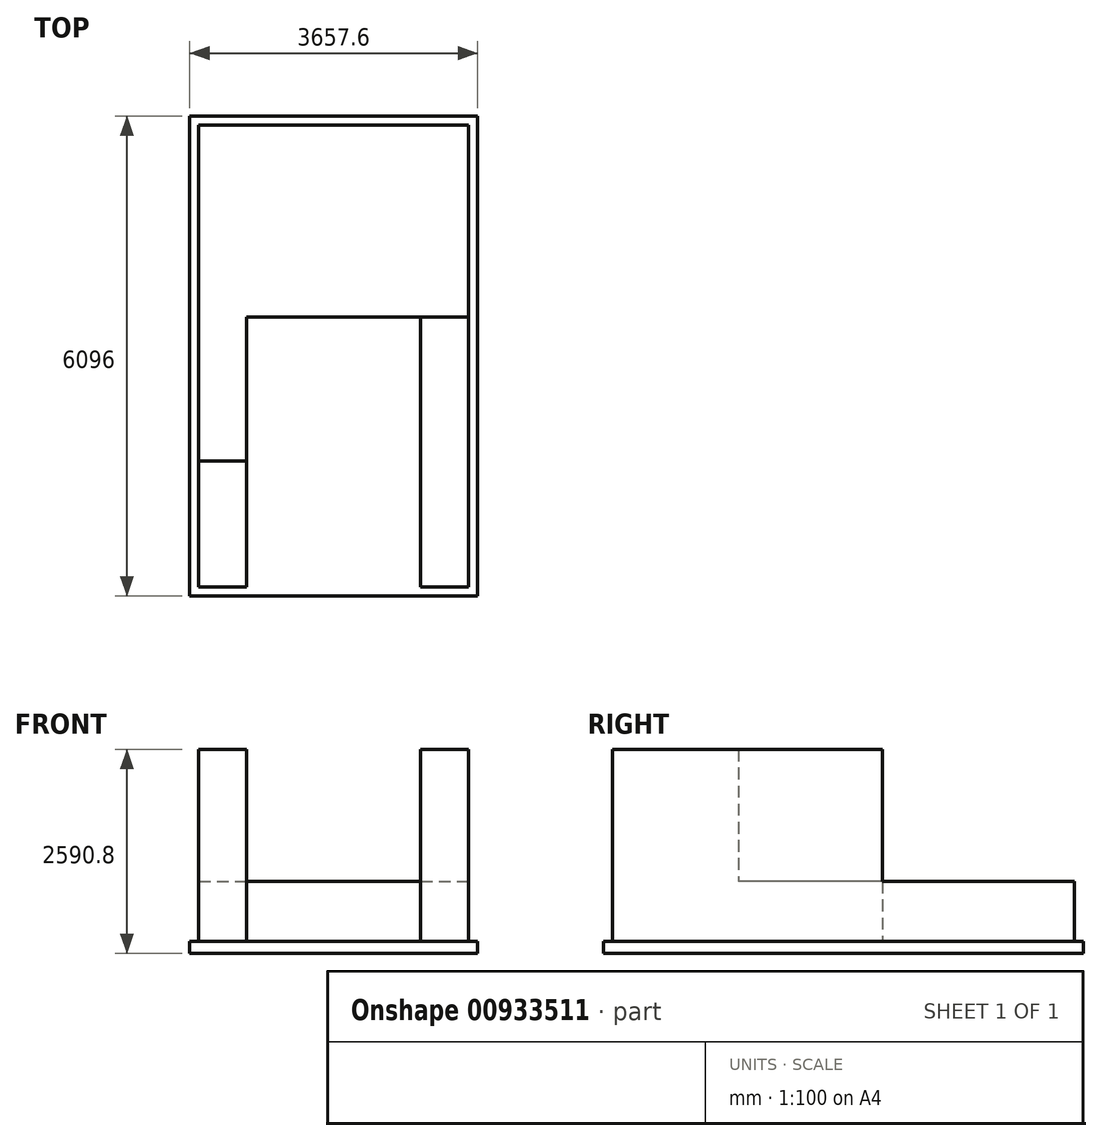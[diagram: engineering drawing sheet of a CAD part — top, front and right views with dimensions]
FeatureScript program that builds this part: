
annotation { "Feature Type Name" : "Feature", "Feature Type Description" : "" }
export const myFeature = defineFeature(function(context is Context, id is Id, definition is map)
    precondition{}
    {
        {
            var Q0;
            Q0=qCreatedBy(makeId("Top.planeOp"),FACE);
            var sketch = newSketch(context, id + "F0", { "sketchPlane" : qUnion([Q0])});
            skLineSegment(sketch, "E0.bottom", {"start": v(0, 0) * mm, "end": v(3657.6, 0) * mm});
            skLineSegment(sketch, "E0.top", {"start": v(0, 6096) * mm, "end": v(3657.6, 6096) * mm});
            skLineSegment(sketch, "E0.left", {"start": v(0, 0) * mm, "end": v(0, 6096) * mm});
            skLineSegment(sketch, "E0.right", {"start": v(3657.6, 0) * mm, "end": v(3657.6, 6096) * mm});
            skSolve(sketch);
        }
        {
            var Q0;
            Q0=makeQuery(id+"F0.imprint","IMPRINT",FACE,{"disambiguationData":[TD([[makeQuery(id+"F0.imprint","IMPRINT",EDGE,{"derivedFrom":sQuery(id+"F0.wireOp",EDGE,"E0.bottom")}),1.0]])]});
            extrude(context, id + "F1", {"entities" : qUnion([Q0]), "depth" : 152.4 * mm, "offsetDistance" : 25.4 * mm});
        }
        {
            var Q0;
            Q0=makeQuery(id+"F1.opExtrude","CAP_FACE",FACE,{"disambiguationData":[OSD([sQuery(id+"F0.wireOp",EDGE,"E0.bottom"),sQuery(id+"F0.wireOp",EDGE,"E0.top"),sQuery(id+"F0.wireOp",EDGE,"E0.left"),sQuery(id+"F0.wireOp",EDGE,"E0.right")])],"isStart":false});
            var sketch = newSketch(context, id + "F2", { "sketchPlane" : qUnion([Q0])});
            skLineSegment(sketch, "E1.bottom", {"start": v(114.3, 5981.7) * mm, "end": v(3543.3, 5981.7) * mm});
            skLineSegment(sketch, "E1.top", {"start": v(114.3, 3543.3) * mm, "end": v(3543.3, 3543.3) * mm});
            skLineSegment(sketch, "E1.left", {"start": v(114.3, 5981.7) * mm, "end": v(114.3, 3543.3) * mm});
            skLineSegment(sketch, "E1.right", {"start": v(3543.3, 5981.7) * mm, "end": v(3543.3, 3543.3) * mm});
            skLineSegment(sketch, "E2.bottom", {"start": v(3543.3, 3543.3) * mm, "end": v(2933.7, 3543.3) * mm});
            skLineSegment(sketch, "E2.top", {"start": v(3543.3, 114.3) * mm, "end": v(2933.7, 114.3) * mm});
            skLineSegment(sketch, "E2.left", {"start": v(3543.3, 3543.3) * mm, "end": v(3543.3, 114.3) * mm});
            skLineSegment(sketch, "E2.right", {"start": v(2933.7, 3543.3) * mm, "end": v(2933.7, 114.3) * mm});
            skLineSegment(sketch, "E3.bottom", {"start": v(114.3, 3543.3) * mm, "end": v(723.9, 3543.3) * mm});
            skLineSegment(sketch, "E3.top", {"start": v(114.3, 1714.5) * mm, "end": v(723.9, 1714.5) * mm});
            skLineSegment(sketch, "E3.left", {"start": v(114.3, 3543.3) * mm, "end": v(114.3, 1714.5) * mm});
            skLineSegment(sketch, "E3.right", {"start": v(723.9, 3543.3) * mm, "end": v(723.9, 1714.5) * mm});
            skLineSegment(sketch, "E4.top", {"start": v(114.3, 114.3) * mm, "end": v(723.9, 114.3) * mm});
            skLineSegment(sketch, "E4.left", {"start": v(114.3, 1714.5) * mm, "end": v(114.3, 114.3) * mm});
            skLineSegment(sketch, "E4.right", {"start": v(723.9, 1714.5) * mm, "end": v(723.9, 114.3) * mm});
            skSolve(sketch);
        }
        {
            var Q0;
            Q0=makeQuery(id+"F2.imprint","IMPRINT",FACE,{"disambiguationData":[TD([[makeQuery(id+"F2.imprint","IMPRINT",EDGE,{"derivedFrom":sQuery(id+"F2.wireOp",EDGE,"E1.bottom")}),-1.0]])]});
            var Q1;
            Q1=makeQuery(id+"F2.imprint","IMPRINT",FACE,{"disambiguationData":[TD([[makeQuery(id+"F2.imprint","IMPRINT",EDGE,{"derivedFrom":sQuery(id+"F2.wireOp",EDGE,"E3.top")}),1.0]])]});
            extrude(context, id + "F3", {"entities" : qUnion([Q0, Q1]), "operationType" : NewBodyOperationType.ADD, "depth" : 762 * mm, "offsetDistance" : 25.4 * mm});
        }
        {
            var Q0;
            Q0=makeQuery(id+"F2.imprint","IMPRINT",FACE,{"disambiguationData":[TD([[makeQuery(id+"F2.imprint","IMPRINT",EDGE,{"derivedFrom":sQuery(id+"F2.wireOp",EDGE,"E3.top")}),-1.0]])]});
            var Q1;
            Q1=makeQuery(id+"F2.imprint","IMPRINT",FACE,{"disambiguationData":[TD([[makeQuery(id+"F2.imprint","IMPRINT",EDGE,{"derivedFrom":sQuery(id+"F2.wireOp",EDGE,"E2.top")}),-1.0]])]});
            extrude(context, id + "F4", {"entities" : qUnion([Q0, Q1]), "operationType" : NewBodyOperationType.ADD, "depth" : 2438.4 * mm, "offsetDistance" : 25.4 * mm});
        }
    });
